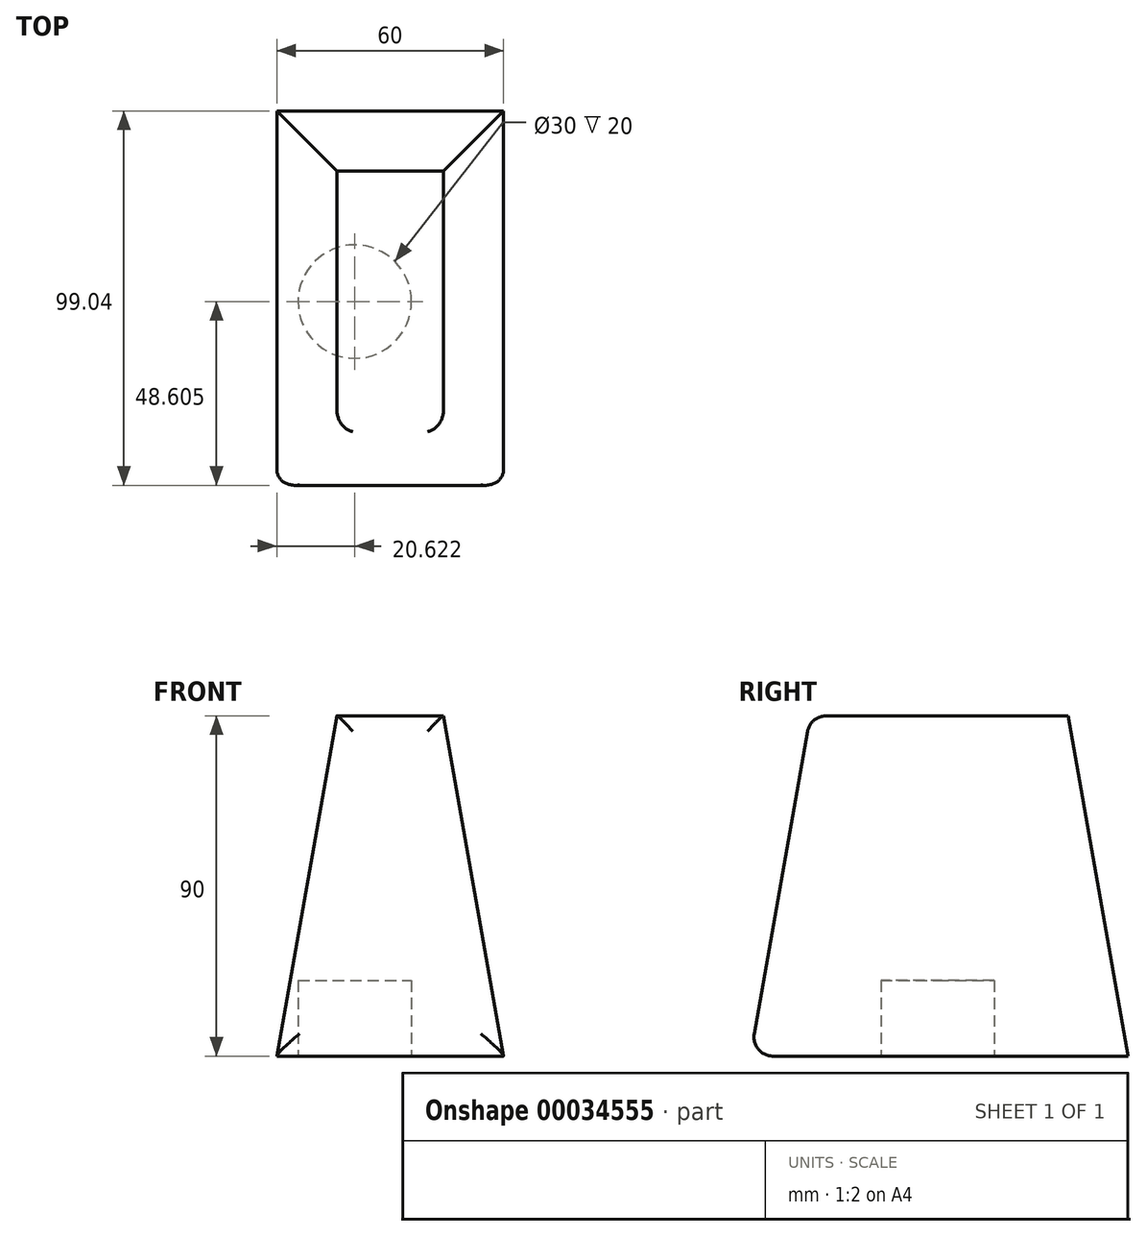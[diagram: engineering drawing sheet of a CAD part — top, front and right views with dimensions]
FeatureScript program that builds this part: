
annotation { "Feature Type Name" : "Feature", "Feature Type Description" : "" }
export const myFeature = defineFeature(function(context is Context, id is Id, definition is map)
    precondition{}
    {
        {
            var Q0;
            Q0=qCreatedBy(makeId("Top.planeOp"),FACE);
            var sketch = newSketch(context, id + "F3", { "sketchPlane" : qUnion([Q0])});
            skLineSegment(sketch, "E0.bottom", {"start": v(0, 100) * mm, "end": v(60, 100) * mm});
            skLineSegment(sketch, "E0.top", {"start": v(0, 0) * mm, "end": v(60, 0) * mm});
            skLineSegment(sketch, "E0.left", {"start": v(0, 100) * mm, "end": v(0, 0) * mm});
            skLineSegment(sketch, "E0.right", {"start": v(60, 100) * mm, "end": v(60, 0) * mm});
            skLineSegment(sketch, "E1", {"start": v(77.94, -120.68) * mm, "end": v(19.77, -111.54) * mm, "construction": true});
            skSolve(sketch);
        }
        {
            var Q0;
            Q0=makeQuery(id+"F3.imprint","IMPRINT",FACE,{"disambiguationData":[TD([[makeQuery(id+"F3.imprint","IMPRINT",EDGE,{"derivedFrom":sQuery(id+"F3.wireOp",EDGE,"E0.bottom")}),-1.0]])]});
            extrude(context, id + "F0", {"entities" : qUnion([Q0]), "depth" : 90 * mm, "hasDraft" : true, "draftAngle" : 10 * degree, "draftPullDirection" : true});
        }
        {
            var Q0;
            Q0=makeQuery(id+"F0.opExtrude","SWEPT_EDGE",EDGE,{"disambiguationData":[OSD([sQuery(id+"F3.wireOp",EDGE,"E0.top"),sQuery(id+"F3.wireOp",EDGE,"E0.right")])]});
            var Q1;
            Q1=makeQuery(id+"F0.opExtrude","SWEPT_FACE",FACE,{"disambiguationData":[OSD([sQuery(id+"F3.wireOp",EDGE,"E0.top")])]});
            fillet(context, id + "F1", {"entities" : qUnion([Q0, Q1]), "radius" : 5 * mm, "tangentPropagation" : true, "allowEdgeOverflow" : false});
        }
        {
            var Q0;
            Q0=makeQuery(id+"F0.opExtrude","CAP_FACE",FACE,{"disambiguationData":[OSD([sQuery(id+"F3.wireOp",EDGE,"E0.bottom"),sQuery(id+"F3.wireOp",EDGE,"E0.top"),sQuery(id+"F3.wireOp",EDGE,"E0.left"),sQuery(id+"F3.wireOp",EDGE,"E0.right")])],"isStart":true});
            var sketch = newSketch(context, id + "F2", { "sketchPlane" : qUnion([Q0])});
            skCircle(sketch, "E2", {"center": v(20.62, -49.57) * mm, "radius": 15 * mm});
            skSolve(sketch);
        }
        {
            var Q0;
            Q0=makeQuery(id+"F2.imprint","IMPRINT",FACE,{"disambiguationData":[TD([[makeQuery(id+"F2.imprint","IMPRINT",EDGE,{"derivedFrom":sQuery(id+"F2.wireOp",EDGE,"E2")}),1.0]])]});
            extrude(context, id + "F4", {"entities" : qUnion([Q0]), "operationType" : NewBodyOperationType.REMOVE, "oppositeDirection" : true, "depth" : 20 * mm, "offsetDistance" : 25 * mm});
        }
    });
